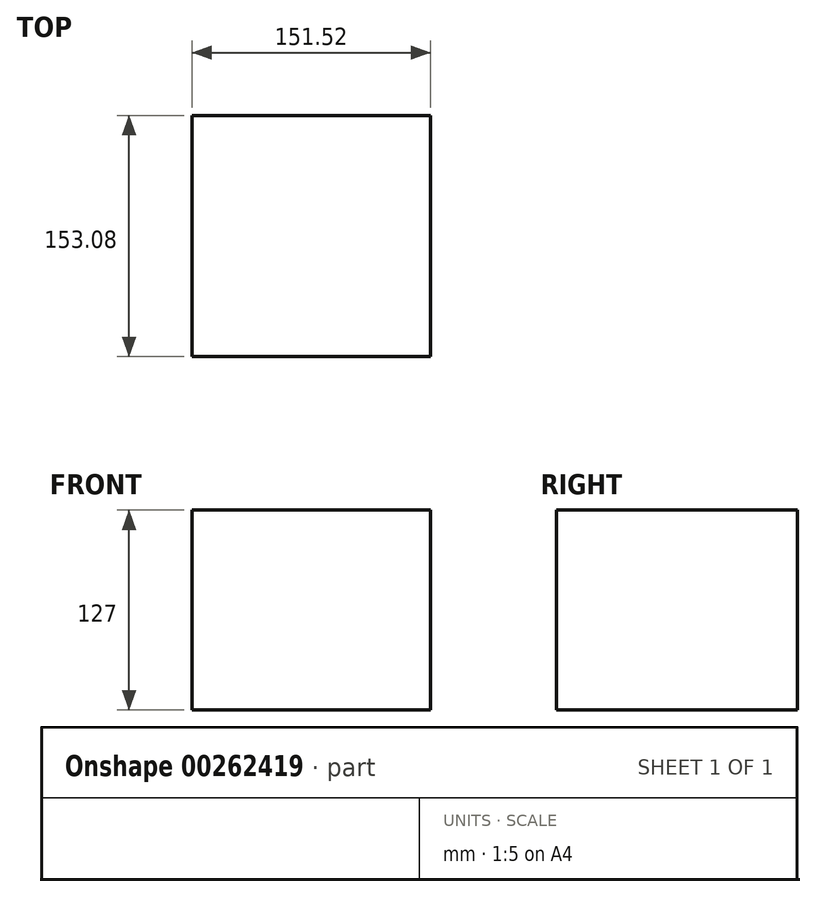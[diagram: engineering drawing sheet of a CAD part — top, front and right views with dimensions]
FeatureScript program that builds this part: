
annotation { "Feature Type Name" : "Feature", "Feature Type Description" : "" }
export const myFeature = defineFeature(function(context is Context, id is Id, definition is map)
    precondition{}
    {
        {
            var Q0;
            Q0=qCreatedBy(makeId("Top.planeOp"),FACE);
            var sketch = newSketch(context, id + "F0", { "sketchPlane" : qUnion([Q0])});
            skLineSegment(sketch, "E0.bottom", {"start": v(75.76, 76.15) * mm, "end": v(-75.76, 76.15) * mm});
            skLineSegment(sketch, "E0.top", {"start": v(75.76, -76.93) * mm, "end": v(-75.76, -76.93) * mm});
            skLineSegment(sketch, "E0.left", {"start": v(75.76, 76.15) * mm, "end": v(75.76, -76.93) * mm});
            skLineSegment(sketch, "E0.right", {"start": v(-75.76, 76.15) * mm, "end": v(-75.76, -76.93) * mm});
            skPoint(sketch, "E0.middle", {"position": v(0, -0.39) * mm});
            skSolve(sketch);
        }
        {
            var Q0;
            Q0=makeQuery(id+"F0.imprint","IMPRINT",FACE,{"disambiguationData":[TD([[makeQuery(id+"F0.imprint","IMPRINT",EDGE,{"derivedFrom":sQuery(id+"F0.wireOp",EDGE,"E0.bottom")}),1.0]])]});
            extrude(context, id + "F1", {"entities" : qUnion([Q0]), "depth" : 127 * mm});
        }
    });
